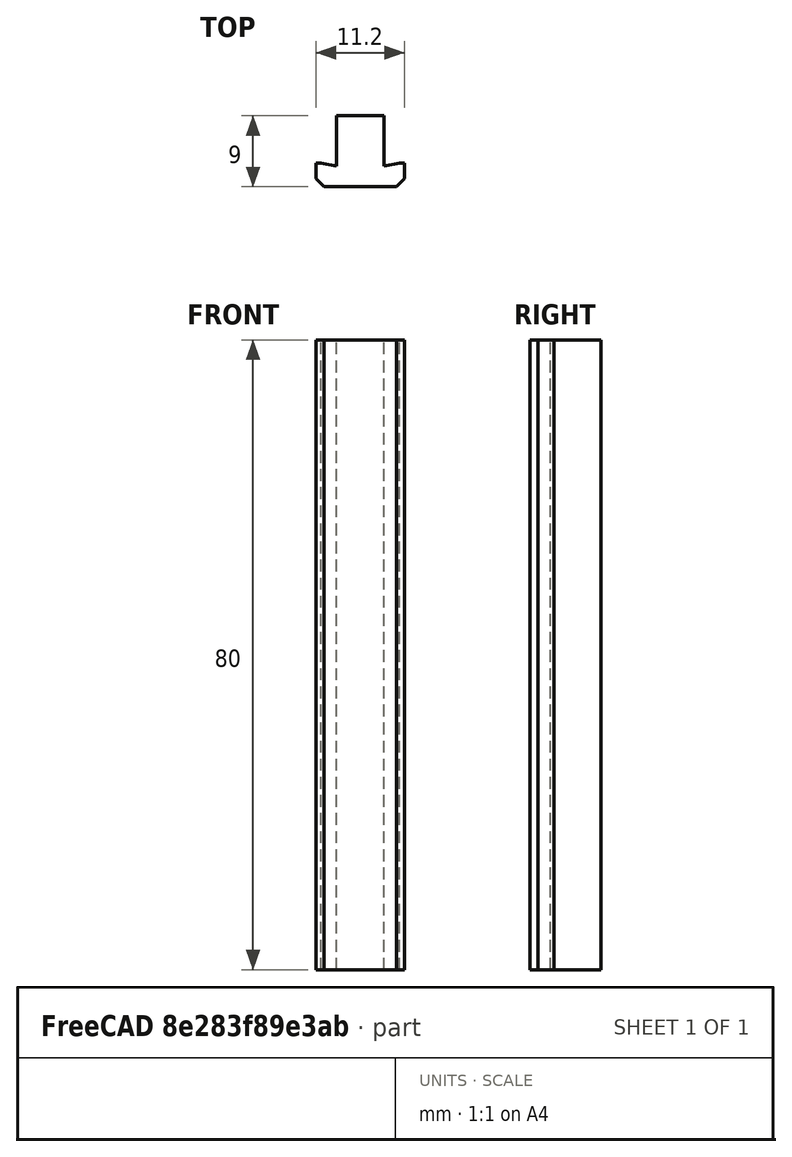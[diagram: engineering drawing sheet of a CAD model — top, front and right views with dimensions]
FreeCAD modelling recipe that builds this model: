
FCSTD DOCUMENT  (FreeCAD 0.19R17798 (Git))
Label: ts4_sub
License: All rights reserved
LicenseURL: http://en.wikipedia.org/wiki/All_rights_reserved
objects: Sketcher::SketchObject×1, PartDesign::Pad×1, PartDesign::Body×1
note: 4 computed .brp shape members not serialized (recipe doc carries the construction recipe); baked Part::Feature solids carry a one-line shape summary decoded from their .brp

FEATURE [Sketcher::SketchObject] Sketch
  MapMode = 5
  Support = -> [XY_Plane]
  sketch-geometry (12):
    g0: LineSegment StartX=0 StartY=3 StartZ=0 EndX=0 EndY=1 EndZ=0
    g1: LineSegment StartX=0 StartY=1 StartZ=0 EndX=1 EndY=0 EndZ=0
    g2: LineSegment StartX=1 StartY=0 StartZ=0 EndX=10.2 EndY=0 EndZ=0
    g3: LineSegment StartX=10.2 StartY=0 StartZ=0 EndX=11.2 EndY=1 EndZ=0
    g4: LineSegment StartX=11.2 StartY=1 StartZ=0 EndX=11.2 EndY=3 EndZ=0
    g5: LineSegment StartX=11.2 StartY=3 StartZ=0 EndX=10.6 EndY=3 EndZ=0
    g6: LineSegment StartX=10.6 StartY=3 StartZ=0 EndX=8.6 EndY=2.6 EndZ=0
    g7: LineSegment StartX=8.6 StartY=2.6 StartZ=0 EndX=8.6 EndY=9 EndZ=0
    g8: LineSegment StartX=8.6 StartY=9 StartZ=0 EndX=2.6 EndY=9 EndZ=0
    g9: LineSegment StartX=2.6 StartY=9 StartZ=0 EndX=2.6 EndY=2.6 EndZ=0
    g10: LineSegment StartX=2.6 StartY=2.6 StartZ=0 EndX=0.6 EndY=3 EndZ=0
    g11: LineSegment StartX=0.6 StartY=3 StartZ=0 EndX=0 EndY=3 EndZ=0
  constraints (36):
    c: Coincident(g0,g1)
    c: Coincident(g1,g2)
    c: Coincident(g2,g3)
    c: Coincident(g3,g4)
    c: Coincident(g4,g5)
    c: Coincident(g5,g6)
    c: Coincident(g6,g7)
    c: Coincident(g7,g8)
    c: Coincident(g8,g9)
    c: Coincident(g9,g10)
    c: Coincident(g10,g11)
    c: Coincident(g11,g0)
    c: DistanceX(g-1,g4) = 11.2
    c: DistanceX(g-1,g8) = 2.6
    c: DistanceX(g8,g8) = 6
    c: DistanceX(g0,g10) = 0.6
    c: DistanceX(g-1,g0) = 0
    c: DistanceX(g0,g-1) = 0
    c: DistanceX(g8,g9) = 0
    c: DistanceY(g-1,g0) = 3
    c: DistanceY(g0,g10) = 0
    c: DistanceY(g-1,g0) = 1
    c: DistanceX(g-1,g1) = 1
    c: DistanceY(g-1,g9) = 2.6
    c: DistanceY(g9,g8) = 6.4
    c: Horizontal(g8)
    c: DistanceX(g6,g7) = 0
    c: DistanceY(g9,g6) = 0
    c: DistanceX(g5,g4) = 0.6
    c: DistanceY(g0,g4) = 0
    c: DistanceY(g4,g5) = 0
    c: DistanceX(g4,g3) = 0
    c: DistanceY(g-1,g1) = 0
    c: DistanceY(g1,g2) = 0
    c: DistanceY(g2,g3) = 1
    c: DistanceX(g2,g3) = 1
FEATURE [PartDesign::Pad] Pad
  Length = 80
  Length2 = 100
  Profile = -> Sketch
  Type = 0
FEATURE [PartDesign::Body] Body
  Group = -> [Sketch,Pad]
  Origin = -> Origin
  Tip = -> Pad
